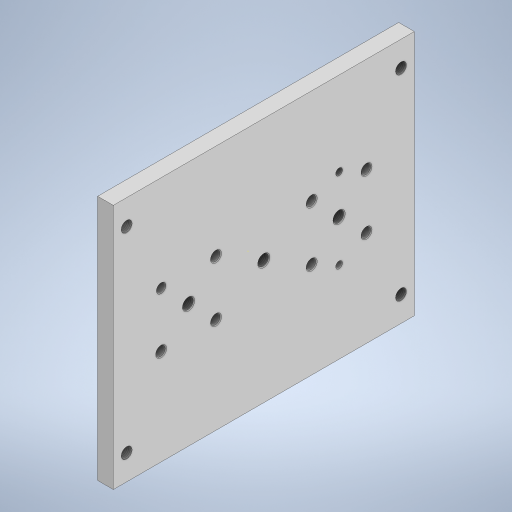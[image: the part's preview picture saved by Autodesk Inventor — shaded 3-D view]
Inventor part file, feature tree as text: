
AUTODESK INVENTOR PART (.ipt)
format: ipt  version: 2023.5 (Build 275446000, 446)  size: 334,336 bytes
history: native  units: mm
features: thread x9, sketch x5, extrude x3, chamfer x3, hole x1
ambient origin geometry x8: Origin, YZ Plane, XZ Plane, XY Plane, X Axis, Y Axis, Z Axis, Center Point
bodies: Volumenkörper1 (feature_tree)
feature tree (21):
  extrude  "Extrusion1"  Depth=157.0mm
  sketch  "草图5"  dims[d2=78.5mm d3=96.0mm d4=10.0mm d5=0.0mm]
  hole  "孔1"  [1 undecoded]
  chamfer  "倒角1"  Distance=10.0mm
  extrude  "拉伸4"  Depth=48.0mm
  chamfer  "倒角3"  Distance=35.0mm
  thread  "螺纹3"  [1 undecoded]
  thread  "螺纹4"  [1 undecoded]
  thread  "螺纹5"  [1 undecoded]
  extrude  "拉伸5"  Depth=10.0mm
  chamfer  "倒角4"  Distance=5.0mm
  thread  "螺纹6"  [1 undecoded]
  thread  "螺纹7"  [1 undecoded]
  thread  "螺纹8"  [1 undecoded]
  thread  "螺纹9"  [1 undecoded]
  thread  "螺纹10"  [1 undecoded]
  thread  "螺纹11"  [1 undecoded]
  sketch  "Skizze1"  dims[d0=192.0mm d1=157.0mm]
  sketch  "草图6"  dims[d31=50.0mm d32=48.0mm]
  sketch  "草图7"  dims[d33=24.0mm]
  sketch  "草图8"  dims[d34=35.0mm d35=35.0mm d36=5.0mm d37=40.0mm d39=360.0deg d41=6.0mm d42=12.0mm d43=4.0mm d44=2.0mm d45=90.0deg d46=8.0mm d47=20.594885mm d48=5.0mm d49=5.0mm d50=5.0mm d51=5.0mm d52=0.5mm d53=2.0mm d54=45.0deg d58=6.8mm d59=6.8mm d60=6.8mm d61=10.0mm d62=0.0mm d63=0.5mm d64=2.0mm d65=45.0deg d66=10.0mm d67=0.0mm d68=10.0mm d69=0.0mm d70=10.0mm d71=0.0mm d72=175.0mm d73=125.0mm d74=6.5mm d75=10.0mm d76=0.0mm d77=0.2mm d78=2.0mm d79=45.0deg d80=10.0mm d81=0.0mm d82=10.0mm d83=0.0mm d84=10.0mm d85=0.0mm d86=10.0mm d87=0.0mm d89=30.0mm d90=4.3mm d91=10.0mm d92=0.0mm d93=10.0mm d94=0.0mm d95=25.3mm d55=0.75mm d56=20.594885mm d57=0.0625mm]
note: 10 required parameter values undecoded (feature->parameter linkage not recoverable at this tier; creation-order binding heuristic only, values carry confidence <= 0.55)
